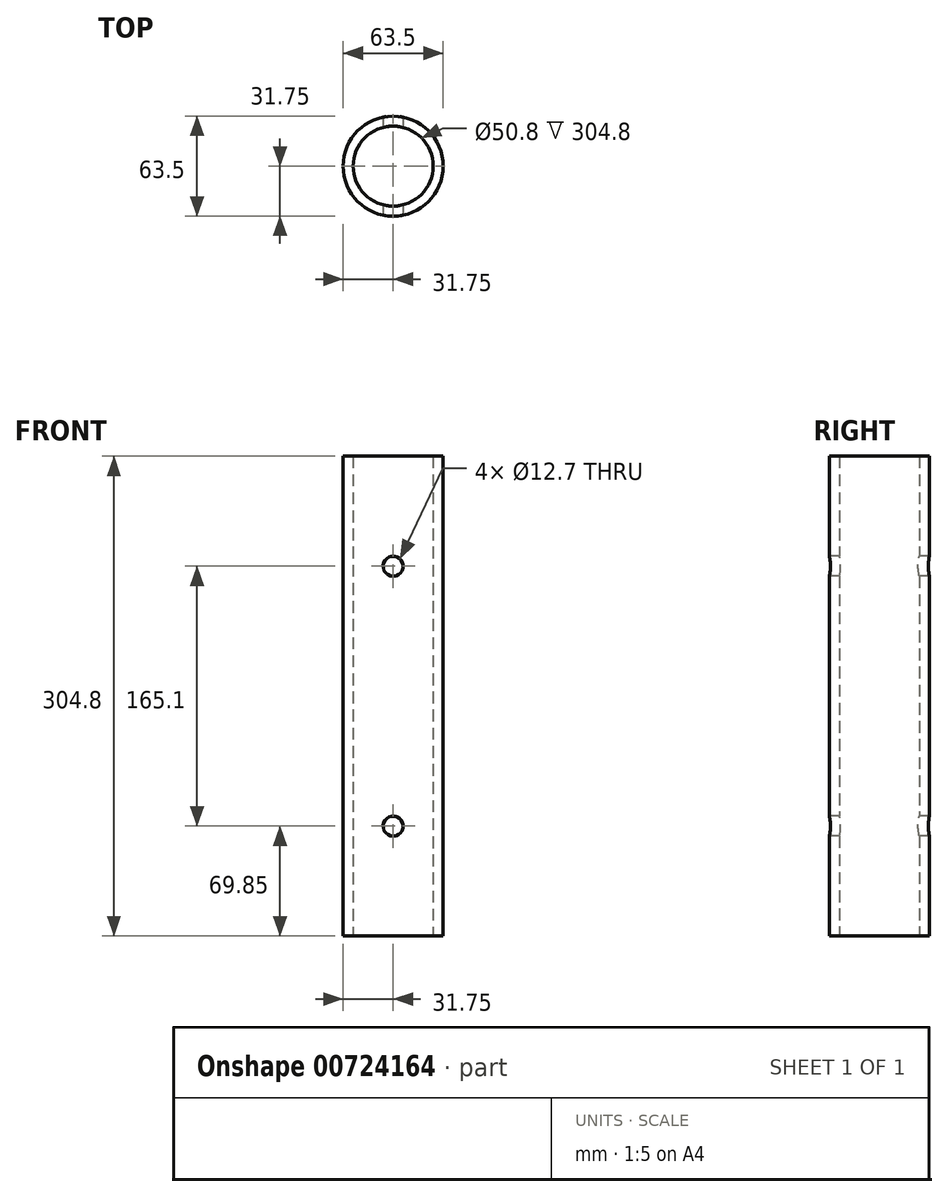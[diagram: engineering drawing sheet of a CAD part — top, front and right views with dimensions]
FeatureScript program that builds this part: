
annotation { "Feature Type Name" : "Feature", "Feature Type Description" : "" }
export const myFeature = defineFeature(function(context is Context, id is Id, definition is map)
    precondition{}
    {
        {
            var Q0;
            Q0=qCreatedBy(makeId("Top.planeOp"),FACE);
            var sketch = newSketch(context, id + "F0", { "sketchPlane" : qUnion([Q0])});
            skCircle(sketch, "E0", {"center": v(0, 0) * mm, "radius": 31.75 * mm});
            skSolve(sketch);
        }
        {
            var Q0;
            Q0=makeQuery(id+"F0.imprint","IMPRINT",FACE,{"disambiguationData":[TD([[makeQuery(id+"F0.imprint","IMPRINT",EDGE,{"derivedFrom":sQuery(id+"F0.wireOp",EDGE,"E0")}),1.0]])]});
            extrude(context, id + "F1", {"entities" : qUnion([Q0]), "depth" : 304.8 * mm, "offsetDistance" : 25.4 * mm, "symmetric" : true});
        }
        {
            var Q0;
            Q0=makeQuery(id+"F1.opExtrude","CAP_FACE",FACE,{"disambiguationData":[OSD([sQuery(id+"F0.wireOp",EDGE,"E0")])],"isStart":true});
            var sketch = newSketch(context, id + "F2", { "sketchPlane" : qUnion([Q0])});
            skCircle(sketch, "E1", {"center": v(0, 0) * mm, "radius": 25.4 * mm});
            skSolve(sketch);
        }
        {
            var Q0;
            Q0 = qSketchRegion(id + "F2", true);
            extrude(context, id + "F3", {"entities" : qUnion([Q0]), "operationType" : NewBodyOperationType.REMOVE, "oppositeDirection" : true, "depth" : 304.8 * mm, "offsetDistance" : 25.4 * mm});
        }
        {
            var Q0;
            Q0=qCreatedBy(makeId("Front.planeOp"),FACE);
            var sketch = newSketch(context, id + "F4", { "sketchPlane" : qUnion([Q0])});
            skLineSegment(sketch, "E2", {"start": v(0, 0) * mm, "end": v(0, 82.55) * mm, "construction": true});
            skLineSegment(sketch, "E3", {"start": v(0, 0) * mm, "end": v(0, -82.55) * mm, "construction": true});
            skCircle(sketch, "E4", {"center": v(0, 82.55) * mm, "radius": 6.35 * mm});
            skCircle(sketch, "E5", {"center": v(0, -82.55) * mm, "radius": 6.35 * mm});
            skSolve(sketch);
        }
        {
            var Q0;
            Q0 = qSketchRegion(id + "F4", true);
            extrude(context, id + "F5", {"entities" : qUnion([Q0]), "operationType" : NewBodyOperationType.REMOVE, "oppositeDirection" : true, "depth" : 63.5 * mm, "offsetDistance" : 25.4 * mm, "symmetric" : true});
        }
    });
